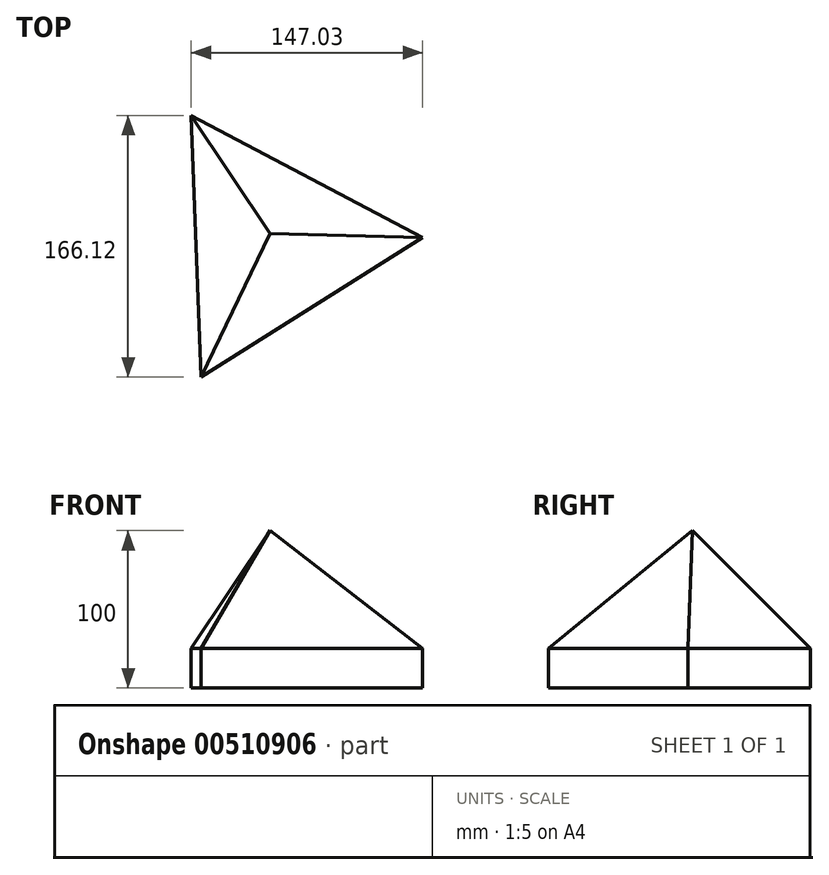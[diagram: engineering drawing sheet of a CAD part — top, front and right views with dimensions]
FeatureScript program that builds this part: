
annotation { "Feature Type Name" : "Feature", "Feature Type Description" : "" }
export const myFeature = defineFeature(function(context is Context, id is Id, definition is map)
    precondition{}
    {
        {
            var Q0;
            Q0=qCreatedBy(makeId("Top.planeOp"),FACE);
            var sketch = newSketch(context, id + "F0", { "sketchPlane" : qUnion([Q0])});
            skCircle(sketch, "E0.cCircle", {"center": v(-1.72, 4.45) * mm, "radius": 95.98 * mm, "construction": true});
            skLineSegment(sketch, "E0.0", {"start": v(-46.5, -80.44) * mm, "end": v(-52.84, 85.68) * mm});
            skLineSegment(sketch, "E0.1", {"start": v(-52.84, 85.68) * mm, "end": v(94.19, 8.1) * mm});
            skLineSegment(sketch, "E0.2", {"start": v(94.19, 8.1) * mm, "end": v(-46.5, -80.44) * mm});
            skSolve(sketch);
        }
        {
            var Q0;
            Q0=makeQuery(id+"F0.imprint","IMPRINT",FACE,{"disambiguationData":[TD([[makeQuery(id+"F0.imprint","IMPRINT",EDGE,{"derivedFrom":sQuery(id+"F0.wireOp",EDGE,"E0.0")}),-1.0]])]});
            extrude(context, id + "F1", {"entities" : qUnion([Q0]), "depth" : 25 * mm});
        }
        {
            var Q0;
            Q0=qCreatedBy(makeId("Top.planeOp"),FACE);
            cPlane(context, id + "F2", {"entities" : qUnion([Q0]), "cplaneType" : CPlaneType.OFFSET, "offset" : 100 * mm, "width" : 150 * mm, "height" : 150 * mm});
        }
        {
            var Q0;
            Q0=qCreatedBy(id+"F2.planeOp",FACE);
            var sketch = newSketch(context, id + "F3", { "sketchPlane" : qUnion([Q0])});
            skPoint(sketch, "E1", {"position": v(-2.8, 10.72) * mm});
            skSolve(sketch);
        }
        {
            var Q1;
            Q1=sQuery(id+"F3.wireOp",VERTEX,"E1");
            var Q2;
            Q2=makeQuery(id+"F1.opExtrude","CAP_FACE",FACE,{"disambiguationData":[OSD([sQuery(id+"F0.wireOp",EDGE,"E0.0"),sQuery(id+"F0.wireOp",EDGE,"E0.1"),sQuery(id+"F0.wireOp",EDGE,"E0.2")])],"isStart":false});
            loft(context, id + "F4", {"operationType" : NewBodyOperationType.ADD, "sheetProfilesArray" : [{ "sheetProfileEntities" : qUnion([Q1]) }, { "sheetProfileEntities" : qUnion([Q2]) }]});
        }
    });
